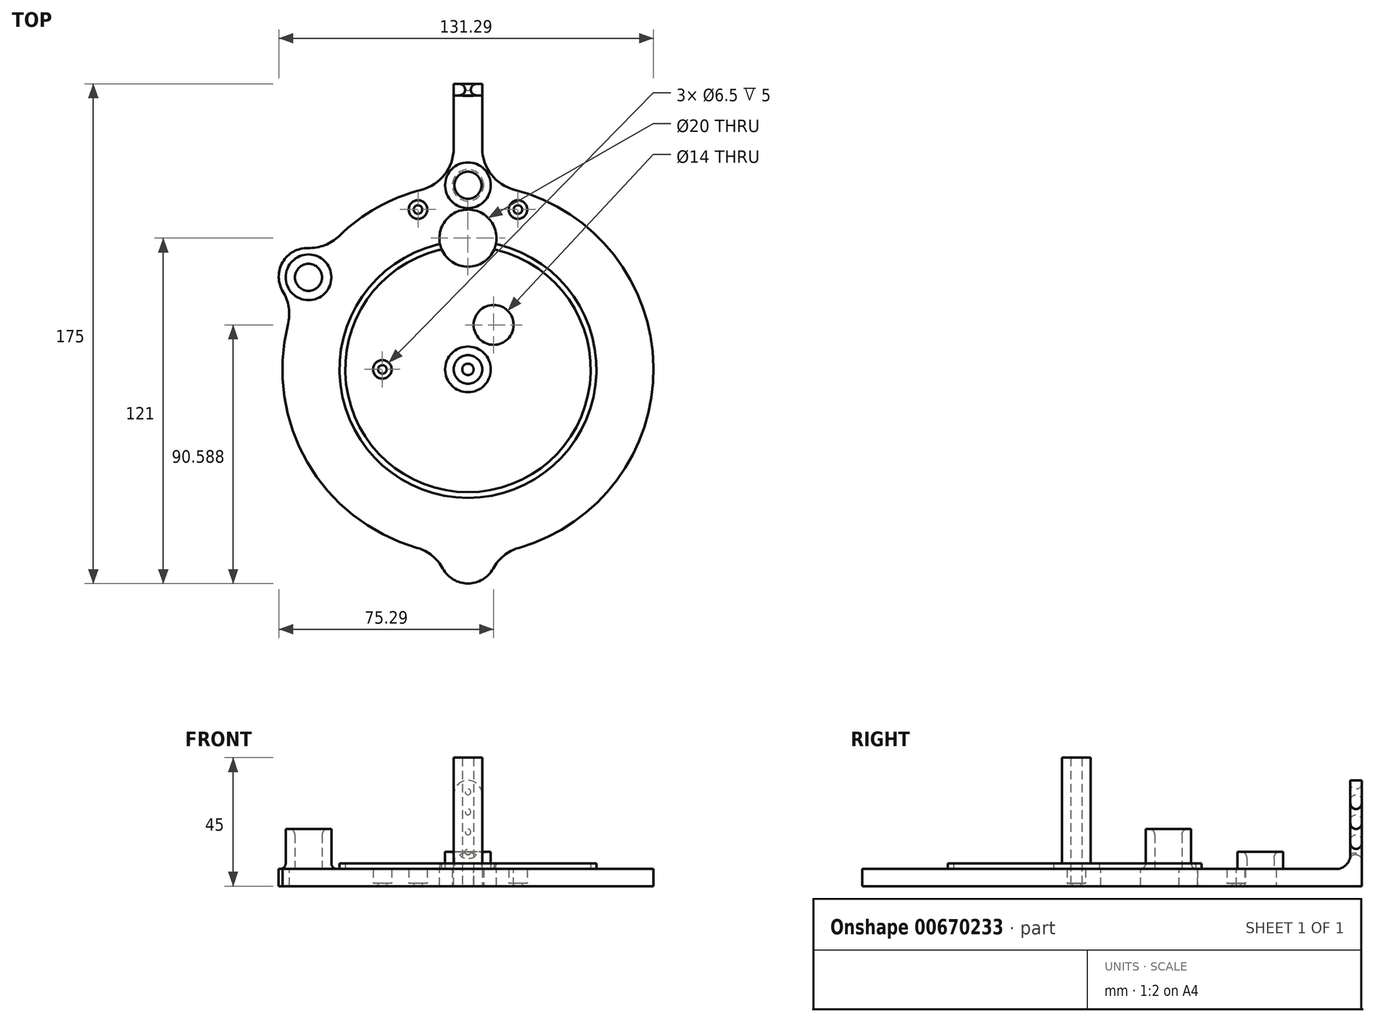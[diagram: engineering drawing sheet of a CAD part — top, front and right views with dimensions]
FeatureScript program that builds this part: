
annotation { "Feature Type Name" : "Feature", "Feature Type Description" : "" }
export const myFeature = defineFeature(function(context is Context, id is Id, definition is map)
    precondition{}
    {
        {
            var Q0;
            Q0=qCreatedBy(makeId("Top.planeOp"),FACE);
            var sketch = newSketch(context, id + "F0", { "sketchPlane" : qUnion([Q0])});
            skCircle(sketch, "E0", {"center": v(0, 0) * mm, "radius": 100 * mm, "construction": true});
            skCircle(sketch, "E1", {"center": v(0, 0) * mm, "radius": 65 * mm});
            skLineSegment(sketch, "E2", {"start": v(0, 0) * mm, "end": v(-56.3, 32.5) * mm, "construction": true});
            skCircle(sketch, "E3", {"center": v(-56.3, 32.5) * mm, "radius": 10 * mm});
            skCircle(sketch, "E4", {"center": v(0, -65) * mm, "radius": 10 * mm});
            skLineSegment(sketch, "E5", {"start": v(0, -65) * mm, "end": v(0, 0) * mm, "construction": true});
            skSolve(sketch);
        }
        {
            var Q0;
            Q0 = qSketchRegion(id + "F0", true);
            extrude(context, id + "F1", {"entities" : qUnion([Q0]), "depth" : 6 * mm, "offsetDistance" : 25 * mm});
        }
        {
            var Q0;
            Q0=qCreatedBy(makeId("Top.planeOp"),FACE);
            var sketch = newSketch(context, id + "F2", { "sketchPlane" : qUnion([Q0])});
            skCircle(sketch, "E6", {"center": v(0, 0) * mm, "radius": 5 * mm});
            skSolve(sketch);
        }
        {
            var Q0;
            Q0 = qSketchRegion(id + "F2", true);
            extrude(context, id + "F3", {"entities" : qUnion([Q0]), "operationType" : NewBodyOperationType.ADD, "depth" : 45 * mm, "offsetDistance" : 25 * mm});
        }
        {
            var Q0;
            Q0=qCreatedBy(makeId("Top.planeOp"),FACE);
            var sketch = newSketch(context, id + "F4", { "sketchPlane" : qUnion([Q0])});
            skCircle(sketch, "E7", {"center": v(0, 0) * mm, "radius": 2 * mm});
            skSolve(sketch);
        }
        {
            var Q0;
            Q0 = qSketchRegion(id + "F4", true);
            extrude(context, id + "F5", {"entities" : qUnion([Q0]), "operationType" : NewBodyOperationType.REMOVE, "depth" : 100 * mm, "offsetDistance" : 25 * mm});
        }
        {
            var Q0;
            Q0=qCreatedBy(makeId("Right.planeOp"),FACE);
            var sketch = newSketch(context, id + "F6", { "sketchPlane" : qUnion([Q0])});
            skLineSegment(sketch, "E8", {"start": v(32.02, 0) * mm, "end": v(100, 0) * mm});
            skLineSegment(sketch, "E9", {"start": v(100, 0) * mm, "end": v(100, 37) * mm});
            skPoint(sketch, "E10.visualSharp", {"position": v(100, 0) * mm});
            skLineSegment(sketch, "E10.filletArc", {"start": v(100, 0) * mm, "end": v(100, 0) * mm});
            skLineSegment(sketch, "E11", {"start": v(32.02, 0) * mm, "end": v(32.02, 6) * mm});
            skLineSegment(sketch, "E12", {"start": v(32.02, 6) * mm, "end": v(91, 6) * mm});
            skLineSegment(sketch, "E13", {"start": v(96, 11) * mm, "end": v(96, 37) * mm});
            skLineSegment(sketch, "E14", {"start": v(96, 37) * mm, "end": v(100, 37) * mm});
            skPoint(sketch, "E15.visualSharp", {"position": v(96, 6) * mm});
            skArc(sketch, "E15.filletArc", {"start": v(91, 6) * mm, "mid": v(94.54, 7.46) * mm, "end": v(96, 11) * mm});
            skSolve(sketch);
        }
        {
            var Q0;
            Q0=makeQuery(id+"F6.imprint","IMPRINT",FACE,{"disambiguationData":[TD([[makeQuery(id+"F6.imprint","IMPRINT",EDGE,{"derivedFrom":sQuery(id+"F6.wireOp",EDGE,"E8")}),1.0]])]});
            extrude(context, id + "F7", {"entities" : qUnion([Q0]), "operationType" : NewBodyOperationType.ADD, "endBound" : BoundingType.SYMMETRIC, "depth" : 10 * mm, "offsetDistance" : 25 * mm});
        }
        {
            var Q0;
            Q0=qCreatedBy(makeId("Front.planeOp"),FACE);
            var sketch = newSketch(context, id + "F8", { "sketchPlane" : qUnion([Q0])});
            skCircle(sketch, "E16", {"center": v(0, 12) * mm, "radius": 1 * mm});
            skCircle(sketch, "E17", {"center": v(0, 19) * mm, "radius": 1 * mm});
            skCircle(sketch, "E18", {"center": v(0, 26) * mm, "radius": 1 * mm});
            skCircle(sketch, "E19", {"center": v(0, 33) * mm, "radius": 1 * mm});
            skSolve(sketch);
        }
        {
            var Q0;
            Q0 = qSketchRegion(id + "F8", true);
            extrude(context, id + "F9", {"entities" : qUnion([Q0]), "operationType" : NewBodyOperationType.REMOVE, "oppositeDirection" : true, "depth" : 200 * mm, "offsetDistance" : 25 * mm, "hasSecondDirection" : true, "secondDirectionOppositeDirection" : true, "secondDirectionDepth" : 50 * mm});
        }
        {
            var Q0;
            Q0=makeQuery(id+"F7.opExtrude","CAP_EDGE",EDGE,{"disambiguationData":[OSD([sQuery(id+"F6.wireOp",EDGE,"E14")])],"isStart":true});
            var Q1;
            Q1=makeQuery(id+"F7.opExtrude","CAP_EDGE",EDGE,{"disambiguationData":[OSD([sQuery(id+"F6.wireOp",EDGE,"E14")])],"isStart":false});
            var Q2;
            Q2=makeQuery(id+"FA8SAaLpnDRHzi7_1.2.F7.opExtrude","CAP_EDGE",EDGE,{"disambiguationData":[OSD([sQuery(id+"F6.wireOp",EDGE,"E14")])],"isStart":true});
            var Q3;
            Q3=makeQuery(id+"FA8SAaLpnDRHzi7_1.2.F7.opExtrude","CAP_EDGE",EDGE,{"disambiguationData":[OSD([sQuery(id+"F6.wireOp",EDGE,"E14")])],"isStart":false});
            var Q4;
            Q4=makeQuery(id+"FA8SAaLpnDRHzi7_1.1.F7.opExtrude","CAP_EDGE",EDGE,{"disambiguationData":[OSD([sQuery(id+"F6.wireOp",EDGE,"E14")])],"isStart":true});
            var Q5;
            Q5=makeQuery(id+"FA8SAaLpnDRHzi7_1.1.F7.opExtrude","CAP_EDGE",EDGE,{"disambiguationData":[OSD([sQuery(id+"F6.wireOp",EDGE,"E14")])],"isStart":false});
            fillet(context, id + "F10", {"entities" : qUnion([Q0, Q1, Q2, Q3, Q4, Q5]), "radius" : 5 * mm, "tangentPropagation" : true, "allowEdgeOverflow" : false});
        }
        {
            var Q0;
            Q0=makeQuery(id+"FA8SAaLpnDRHzi7_1.1.F7.boolean.opBoolean","INTERSECT",EDGE,{"derivedFrom":[makeQuery(id+"F1.opExtrude","SWEPT_FACE",FACE,{"disambiguationData":[OSD([sQuery(id+"F0.wireOp",EDGE,"E1")])]}),makeQuery(id+"FA8SAaLpnDRHzi7_1.1.F7.opExtrude","CAP_FACE",FACE,{"disambiguationData":[OSD([sQuery(id+"F6.wireOp",EDGE,"E8"),sQuery(id+"F6.wireOp",EDGE,"E9"),sQuery(id+"F6.wireOp",EDGE,"E10.filletArc"),sQuery(id+"F6.wireOp",EDGE,"E11"),sQuery(id+"F6.wireOp",EDGE,"E12"),sQuery(id+"F6.wireOp",EDGE,"E13"),sQuery(id+"F6.wireOp",EDGE,"E14"),sQuery(id+"F6.wireOp",EDGE,"E15.filletArc")])],"isStart":true})]});
            var Q1;
            {var subQ0=sQuery(id+"F6.wireOp",EDGE,"E15.filletArc");var subQ1=sQuery(id+"F6.wireOp",EDGE,"E14");var subQ2=sQuery(id+"F6.wireOp",EDGE,"E13");var subQ3=sQuery(id+"F6.wireOp",EDGE,"E12");var subQ4=sQuery(id+"F6.wireOp",EDGE,"E11");var subQ5=sQuery(id+"F6.wireOp",EDGE,"E10.filletArc");var subQ6=sQuery(id+"F6.wireOp",EDGE,"E9");var subQ7=sQuery(id+"F6.wireOp",EDGE,"E8");var subQ8=sQuery(id+"F0.wireOp",EDGE,"E1");Q1=makeQuery(id+"FA8SAaLpnDRHzi7_1.2.F7.boolean.opBoolean","INTERSECT",EDGE,{"derivedFrom":[makeQuery(id+"FA8SAaLpnDRHzi7_1.1.F7.boolean.opBoolean","SPLIT",FACE,{"disambiguationData":[TD([makeQuery(id+"F7.opExtrude","CAP_FACE",FACE,{"disambiguationData":[OSD([subQ7,subQ6,subQ5,subQ4,subQ3,subQ2,subQ1,subQ0])],"isStart":false})])],"derivedFrom":makeQuery(id+"F1.opExtrude","SWEPT_FACE",FACE,{"disambiguationData":[OSD([subQ8])]})}),makeQuery(id+"FA8SAaLpnDRHzi7_1.2.F7.opExtrude","CAP_FACE",FACE,{"disambiguationData":[OSD([subQ7,subQ6,subQ5,subQ4,subQ3,subQ2,subQ1,subQ0])],"isStart":false})]});}
            var Q2;
            {var subQ0=sQuery(id+"F6.wireOp",EDGE,"E15.filletArc");var subQ1=sQuery(id+"F6.wireOp",EDGE,"E14");var subQ2=sQuery(id+"F6.wireOp",EDGE,"E13");var subQ3=sQuery(id+"F6.wireOp",EDGE,"E12");var subQ4=sQuery(id+"F6.wireOp",EDGE,"E11");var subQ5=sQuery(id+"F6.wireOp",EDGE,"E10.filletArc");var subQ6=sQuery(id+"F6.wireOp",EDGE,"E9");var subQ7=sQuery(id+"F6.wireOp",EDGE,"E8");var subQ8=sQuery(id+"F0.wireOp",EDGE,"E1");Q2=makeQuery(id+"FA8SAaLpnDRHzi7_1.2.F7.boolean.opBoolean","INTERSECT",EDGE,{"derivedFrom":[makeQuery(id+"FA8SAaLpnDRHzi7_1.1.F7.boolean.opBoolean","SPLIT",FACE,{"disambiguationData":[TD([makeQuery(id+"F7.opExtrude","CAP_FACE",FACE,{"disambiguationData":[OSD([subQ7,subQ6,subQ5,subQ4,subQ3,subQ2,subQ1,subQ0])],"isStart":false})])],"derivedFrom":makeQuery(id+"F1.opExtrude","SWEPT_FACE",FACE,{"disambiguationData":[OSD([subQ8])]})}),makeQuery(id+"FA8SAaLpnDRHzi7_1.2.F7.opExtrude","CAP_FACE",FACE,{"disambiguationData":[OSD([subQ7,subQ6,subQ5,subQ4,subQ3,subQ2,subQ1,subQ0])],"isStart":true})]});}
            var Q3;
            Q3=makeQuery(id+"F7.boolean.opBoolean","INTERSECT",EDGE,{"derivedFrom":[makeQuery(id+"F1.opExtrude","SWEPT_FACE",FACE,{"disambiguationData":[OSD([sQuery(id+"F0.wireOp",EDGE,"E1")])]}),makeQuery(id+"F7.opExtrude","CAP_FACE",FACE,{"disambiguationData":[OSD([sQuery(id+"F6.wireOp",EDGE,"E8"),sQuery(id+"F6.wireOp",EDGE,"E9"),sQuery(id+"F6.wireOp",EDGE,"E10.filletArc"),sQuery(id+"F6.wireOp",EDGE,"E11"),sQuery(id+"F6.wireOp",EDGE,"E12"),sQuery(id+"F6.wireOp",EDGE,"E13"),sQuery(id+"F6.wireOp",EDGE,"E14"),sQuery(id+"F6.wireOp",EDGE,"E15.filletArc")])],"isStart":false})]});
            var Q4;
            Q4=makeQuery(id+"F7.boolean.opBoolean","INTERSECT",EDGE,{"derivedFrom":[makeQuery(id+"F1.opExtrude","SWEPT_FACE",FACE,{"disambiguationData":[OSD([sQuery(id+"F0.wireOp",EDGE,"E1")])]}),makeQuery(id+"F7.opExtrude","CAP_FACE",FACE,{"disambiguationData":[OSD([sQuery(id+"F6.wireOp",EDGE,"E8"),sQuery(id+"F6.wireOp",EDGE,"E9"),sQuery(id+"F6.wireOp",EDGE,"E10.filletArc"),sQuery(id+"F6.wireOp",EDGE,"E11"),sQuery(id+"F6.wireOp",EDGE,"E12"),sQuery(id+"F6.wireOp",EDGE,"E13"),sQuery(id+"F6.wireOp",EDGE,"E14"),sQuery(id+"F6.wireOp",EDGE,"E15.filletArc")])],"isStart":true})]});
            var Q5;
            Q5=makeQuery(id+"FA8SAaLpnDRHzi7_1.1.F7.boolean.opBoolean","INTERSECT",EDGE,{"derivedFrom":[makeQuery(id+"F1.opExtrude","SWEPT_FACE",FACE,{"disambiguationData":[OSD([sQuery(id+"F0.wireOp",EDGE,"E1")])]}),makeQuery(id+"FA8SAaLpnDRHzi7_1.1.F7.opExtrude","CAP_FACE",FACE,{"disambiguationData":[OSD([sQuery(id+"F6.wireOp",EDGE,"E8"),sQuery(id+"F6.wireOp",EDGE,"E9"),sQuery(id+"F6.wireOp",EDGE,"E10.filletArc"),sQuery(id+"F6.wireOp",EDGE,"E11"),sQuery(id+"F6.wireOp",EDGE,"E12"),sQuery(id+"F6.wireOp",EDGE,"E13"),sQuery(id+"F6.wireOp",EDGE,"E14"),sQuery(id+"F6.wireOp",EDGE,"E15.filletArc")])],"isStart":false})]});
            var Q6;
            {var subQ0=sQuery(id+"F0.wireOp",EDGE,"E3");var subQ1=sQuery(id+"F0.wireOp",EDGE,"E1");Q6=makeQuery(id+"F1.opExtrude","SWEPT_EDGE",EDGE,{"disambiguationData":[OSD([subQ1,subQ0]),TDD([makeQuery(id+"F0.imprint","INTERSECT",VERTEX,{"disambiguationData":[OD(1.0)],"derivedFrom":[subQ1,subQ0]})])]});}
            var Q7;
            {var subQ0=sQuery(id+"F0.wireOp",EDGE,"E3");var subQ1=sQuery(id+"F0.wireOp",EDGE,"E1");Q7=makeQuery(id+"F1.opExtrude","SWEPT_EDGE",EDGE,{"disambiguationData":[OSD([subQ1,subQ0]),TDD([makeQuery(id+"F0.imprint","INTERSECT",VERTEX,{"disambiguationData":[OD(0.0)],"derivedFrom":[subQ1,subQ0]})])]});}
            var Q8;
            {var subQ0=sQuery(id+"F0.wireOp",EDGE,"E4");var subQ1=sQuery(id+"F0.wireOp",EDGE,"E1");Q8=makeQuery(id+"F1.opExtrude","SWEPT_EDGE",EDGE,{"disambiguationData":[OSD([subQ1,subQ0]),TDD([makeQuery(id+"F0.imprint","INTERSECT",VERTEX,{"disambiguationData":[OD(0.0)],"derivedFrom":[subQ1,subQ0]})])]});}
            var Q9;
            {var subQ0=sQuery(id+"F0.wireOp",EDGE,"E4");var subQ1=sQuery(id+"F0.wireOp",EDGE,"E1");Q9=makeQuery(id+"F1.opExtrude","SWEPT_EDGE",EDGE,{"disambiguationData":[OSD([subQ1,subQ0]),TDD([makeQuery(id+"F0.imprint","INTERSECT",VERTEX,{"disambiguationData":[OD(1.0)],"derivedFrom":[subQ1,subQ0]})])]});}
            fillet(context, id + "F11", {"entities" : qUnion([Q0, Q1, Q2, Q3, Q4, Q5, Q6, Q7, Q8, Q9]), "radius" : 15 * mm, "tangentPropagation" : true, "allowEdgeOverflow" : false});
        }
        {
            var Q0;
            Q0=qCreatedBy(makeId("Top.planeOp"),FACE);
            var sketch = newSketch(context, id + "F12", { "sketchPlane" : qUnion([Q0])});
            skCircle(sketch, "E20", {"center": v(0, 64.5) * mm, "radius": 5.5 * mm});
            skCircle(sketch, "E21", {"center": v(-17.5, 56) * mm, "radius": 1.5 * mm});
            skCircle(sketch, "E22", {"center": v(17.5, 56) * mm, "radius": 1.5 * mm});
            skSolve(sketch);
        }
        {
            var Q0;
            Q0 = qSketchRegion(id + "F12", true);
            extrude(context, id + "F13", {"entities" : qUnion([Q0]), "operationType" : NewBodyOperationType.REMOVE, "depth" : 25 * mm, "offsetDistance" : 25 * mm});
        }
        {
            var Q0;
            Q0=qCreatedBy(makeId("Top.planeOp"),FACE);
            var sketch = newSketch(context, id + "F14", { "sketchPlane" : qUnion([Q0])});
            skCircle(sketch, "E23", {"center": v(0, 64.5) * mm, "radius": 4.75 * mm, "construction": true});
            skCircle(sketch, "E24", {"center": v(-17.5, 56) * mm, "radius": 1.5 * mm, "construction": true});
            skCircle(sketch, "E25", {"center": v(17.5, 56) * mm, "radius": 1.5 * mm, "construction": true});
            skCircle(sketch, "E26.cCircle", {"center": v(-17.5, 56) * mm, "radius": 3.25 * mm});
            skCircle(sketch, "E27.cCircle", {"center": v(17.5, 56) * mm, "radius": 3.25 * mm});
            skCircle(sketch, "E28", {"center": v(0, 0) * mm, "radius": 58.67 * mm, "construction": true});
            skSolve(sketch);
        }
        {
            var Q0;
            Q0 = qSketchRegion(id + "F14", true);
            extrude(context, id + "F15", {"entities" : qUnion([Q0]), "operationType" : NewBodyOperationType.REMOVE, "depth" : 25 * mm, "offsetDistance" : 25 * mm, "hasSecondDirection" : true, "secondDirectionOppositeDirection" : false, "secondDirectionDepth" : 1 * mm});
        }
        {
            var Q0;
            Q0=makeQuery(id+"FA8SAaLpnDRHzi7_1.2.F9.boolean.opBoolean","INTERSECT",EDGE,{"derivedFrom":[makeQuery(id+"FA8SAaLpnDRHzi7_1.2.F7.opExtrude","SWEPT_FACE",FACE,{"disambiguationData":[OSD([sQuery(id+"F6.wireOp",EDGE,"E13")])]}),makeQuery(id+"FA8SAaLpnDRHzi7_1.2.F9.opExtrude","SWEPT_FACE",FACE,{"disambiguationData":[OSD([sQuery(id+"F8.wireOp",EDGE,"E16")])]})]});
            var Q1;
            Q1=makeQuery(id+"FA8SAaLpnDRHzi7_1.2.F9.boolean.opBoolean","INTERSECT",EDGE,{"derivedFrom":[makeQuery(id+"FA8SAaLpnDRHzi7_1.2.F7.opExtrude","SWEPT_FACE",FACE,{"disambiguationData":[OSD([sQuery(id+"F6.wireOp",EDGE,"E13")])]}),makeQuery(id+"FA8SAaLpnDRHzi7_1.2.F9.opExtrude","SWEPT_FACE",FACE,{"disambiguationData":[OSD([sQuery(id+"F8.wireOp",EDGE,"E17")])]})]});
            var Q2;
            Q2=makeQuery(id+"FA8SAaLpnDRHzi7_1.2.F9.boolean.opBoolean","INTERSECT",EDGE,{"derivedFrom":[makeQuery(id+"FA8SAaLpnDRHzi7_1.2.F7.opExtrude","SWEPT_FACE",FACE,{"disambiguationData":[OSD([sQuery(id+"F6.wireOp",EDGE,"E13")])]}),makeQuery(id+"FA8SAaLpnDRHzi7_1.2.F9.opExtrude","SWEPT_FACE",FACE,{"disambiguationData":[OSD([sQuery(id+"F8.wireOp",EDGE,"E18")])]})]});
            var Q3;
            Q3=makeQuery(id+"FA8SAaLpnDRHzi7_1.2.F9.boolean.opBoolean","INTERSECT",EDGE,{"derivedFrom":[makeQuery(id+"FA8SAaLpnDRHzi7_1.2.F7.opExtrude","SWEPT_FACE",FACE,{"disambiguationData":[OSD([sQuery(id+"F6.wireOp",EDGE,"E9")])]}),makeQuery(id+"FA8SAaLpnDRHzi7_1.2.F9.opExtrude","SWEPT_FACE",FACE,{"disambiguationData":[OSD([sQuery(id+"F8.wireOp",EDGE,"E16")])]})]});
            var Q4;
            Q4=makeQuery(id+"FA8SAaLpnDRHzi7_1.2.F9.boolean.opBoolean","INTERSECT",EDGE,{"derivedFrom":[makeQuery(id+"FA8SAaLpnDRHzi7_1.2.F7.opExtrude","SWEPT_FACE",FACE,{"disambiguationData":[OSD([sQuery(id+"F6.wireOp",EDGE,"E9")])]}),makeQuery(id+"FA8SAaLpnDRHzi7_1.2.F9.opExtrude","SWEPT_FACE",FACE,{"disambiguationData":[OSD([sQuery(id+"F8.wireOp",EDGE,"E17")])]})]});
            var Q5;
            Q5=makeQuery(id+"FA8SAaLpnDRHzi7_1.2.F9.boolean.opBoolean","INTERSECT",EDGE,{"derivedFrom":[makeQuery(id+"FA8SAaLpnDRHzi7_1.2.F7.opExtrude","SWEPT_FACE",FACE,{"disambiguationData":[OSD([sQuery(id+"F6.wireOp",EDGE,"E9")])]}),makeQuery(id+"FA8SAaLpnDRHzi7_1.2.F9.opExtrude","SWEPT_FACE",FACE,{"disambiguationData":[OSD([sQuery(id+"F8.wireOp",EDGE,"E18")])]})]});
            var Q6;
            Q6=makeQuery(id+"F9.boolean.opBoolean","INTERSECT",EDGE,{"derivedFrom":[makeQuery(id+"F7.opExtrude","SWEPT_FACE",FACE,{"disambiguationData":[OSD([sQuery(id+"F6.wireOp",EDGE,"E9")])]}),makeQuery(id+"F9.opExtrude","SWEPT_FACE",FACE,{"disambiguationData":[OSD([sQuery(id+"F8.wireOp",EDGE,"E16")])]})]});
            var Q7;
            Q7=makeQuery(id+"F9.boolean.opBoolean","INTERSECT",EDGE,{"derivedFrom":[makeQuery(id+"F7.opExtrude","SWEPT_FACE",FACE,{"disambiguationData":[OSD([sQuery(id+"F6.wireOp",EDGE,"E9")])]}),makeQuery(id+"F9.opExtrude","SWEPT_FACE",FACE,{"disambiguationData":[OSD([sQuery(id+"F8.wireOp",EDGE,"E17")])]})]});
            var Q8;
            Q8=makeQuery(id+"F9.boolean.opBoolean","INTERSECT",EDGE,{"derivedFrom":[makeQuery(id+"F7.opExtrude","SWEPT_FACE",FACE,{"disambiguationData":[OSD([sQuery(id+"F6.wireOp",EDGE,"E9")])]}),makeQuery(id+"F9.opExtrude","SWEPT_FACE",FACE,{"disambiguationData":[OSD([sQuery(id+"F8.wireOp",EDGE,"E18")])]})]});
            var Q9;
            Q9=makeQuery(id+"F9.boolean.opBoolean","INTERSECT",EDGE,{"derivedFrom":[makeQuery(id+"F7.opExtrude","SWEPT_FACE",FACE,{"disambiguationData":[OSD([sQuery(id+"F6.wireOp",EDGE,"E13")])]}),makeQuery(id+"F9.opExtrude","SWEPT_FACE",FACE,{"disambiguationData":[OSD([sQuery(id+"F8.wireOp",EDGE,"E18")])]})]});
            var Q10;
            Q10=makeQuery(id+"F9.boolean.opBoolean","INTERSECT",EDGE,{"derivedFrom":[makeQuery(id+"F7.opExtrude","SWEPT_FACE",FACE,{"disambiguationData":[OSD([sQuery(id+"F6.wireOp",EDGE,"E13")])]}),makeQuery(id+"F9.opExtrude","SWEPT_FACE",FACE,{"disambiguationData":[OSD([sQuery(id+"F8.wireOp",EDGE,"E17")])]})]});
            var Q11;
            Q11=makeQuery(id+"F9.boolean.opBoolean","INTERSECT",EDGE,{"derivedFrom":[makeQuery(id+"F7.opExtrude","SWEPT_FACE",FACE,{"disambiguationData":[OSD([sQuery(id+"F6.wireOp",EDGE,"E13")])]}),makeQuery(id+"F9.opExtrude","SWEPT_FACE",FACE,{"disambiguationData":[OSD([sQuery(id+"F8.wireOp",EDGE,"E16")])]})]});
            var Q12;
            Q12=makeQuery(id+"FA8SAaLpnDRHzi7_1.1.F9.boolean.opBoolean","INTERSECT",EDGE,{"derivedFrom":[makeQuery(id+"FA8SAaLpnDRHzi7_1.1.F7.opExtrude","SWEPT_FACE",FACE,{"disambiguationData":[OSD([sQuery(id+"F6.wireOp",EDGE,"E9")])]}),makeQuery(id+"FA8SAaLpnDRHzi7_1.1.F9.opExtrude","SWEPT_FACE",FACE,{"disambiguationData":[OSD([sQuery(id+"F8.wireOp",EDGE,"E16")])]})]});
            var Q13;
            Q13=makeQuery(id+"FA8SAaLpnDRHzi7_1.1.F9.boolean.opBoolean","INTERSECT",EDGE,{"derivedFrom":[makeQuery(id+"FA8SAaLpnDRHzi7_1.1.F7.opExtrude","SWEPT_FACE",FACE,{"disambiguationData":[OSD([sQuery(id+"F6.wireOp",EDGE,"E9")])]}),makeQuery(id+"FA8SAaLpnDRHzi7_1.1.F9.opExtrude","SWEPT_FACE",FACE,{"disambiguationData":[OSD([sQuery(id+"F8.wireOp",EDGE,"E17")])]})]});
            var Q14;
            Q14=makeQuery(id+"FA8SAaLpnDRHzi7_1.1.F9.boolean.opBoolean","INTERSECT",EDGE,{"derivedFrom":[makeQuery(id+"FA8SAaLpnDRHzi7_1.1.F7.opExtrude","SWEPT_FACE",FACE,{"disambiguationData":[OSD([sQuery(id+"F6.wireOp",EDGE,"E9")])]}),makeQuery(id+"FA8SAaLpnDRHzi7_1.1.F9.opExtrude","SWEPT_FACE",FACE,{"disambiguationData":[OSD([sQuery(id+"F8.wireOp",EDGE,"E18")])]})]});
            var Q15;
            Q15=makeQuery(id+"FA8SAaLpnDRHzi7_1.1.F9.boolean.opBoolean","INTERSECT",EDGE,{"derivedFrom":[makeQuery(id+"FA8SAaLpnDRHzi7_1.1.F7.opExtrude","SWEPT_FACE",FACE,{"disambiguationData":[OSD([sQuery(id+"F6.wireOp",EDGE,"E13")])]}),makeQuery(id+"FA8SAaLpnDRHzi7_1.1.F9.opExtrude","SWEPT_FACE",FACE,{"disambiguationData":[OSD([sQuery(id+"F8.wireOp",EDGE,"E16")])]})]});
            var Q16;
            Q16=makeQuery(id+"FA8SAaLpnDRHzi7_1.1.F9.boolean.opBoolean","INTERSECT",EDGE,{"derivedFrom":[makeQuery(id+"FA8SAaLpnDRHzi7_1.1.F7.opExtrude","SWEPT_FACE",FACE,{"disambiguationData":[OSD([sQuery(id+"F6.wireOp",EDGE,"E13")])]}),makeQuery(id+"FA8SAaLpnDRHzi7_1.1.F9.opExtrude","SWEPT_FACE",FACE,{"disambiguationData":[OSD([sQuery(id+"F8.wireOp",EDGE,"E17")])]})]});
            var Q17;
            Q17=makeQuery(id+"FA8SAaLpnDRHzi7_1.1.F9.boolean.opBoolean","INTERSECT",EDGE,{"derivedFrom":[makeQuery(id+"FA8SAaLpnDRHzi7_1.1.F7.opExtrude","SWEPT_FACE",FACE,{"disambiguationData":[OSD([sQuery(id+"F6.wireOp",EDGE,"E13")])]}),makeQuery(id+"FA8SAaLpnDRHzi7_1.1.F9.opExtrude","SWEPT_FACE",FACE,{"disambiguationData":[OSD([sQuery(id+"F8.wireOp",EDGE,"E18")])]})]});
            var Q18;
            Q18=makeQuery(id+"FA8SAaLpnDRHzi7_1.2.F9.boolean.opBoolean","COPY",FACE,{"derivedFrom":makeQuery(id+"FA8SAaLpnDRHzi7_1.2.F9.opExtrude","SWEPT_FACE",FACE,{"disambiguationData":[OSD([sQuery(id+"F8.wireOp",EDGE,"E19")])]})});
            var Q19;
            Q19=makeQuery(id+"F9.boolean.opBoolean","COPY",FACE,{"derivedFrom":makeQuery(id+"F9.opExtrude","SWEPT_FACE",FACE,{"disambiguationData":[OSD([sQuery(id+"F8.wireOp",EDGE,"E19")])]})});
            var Q20;
            Q20=makeQuery(id+"FA8SAaLpnDRHzi7_1.1.F9.boolean.opBoolean","COPY",FACE,{"derivedFrom":makeQuery(id+"FA8SAaLpnDRHzi7_1.1.F9.opExtrude","SWEPT_FACE",FACE,{"disambiguationData":[OSD([sQuery(id+"F8.wireOp",EDGE,"E19")])]})});
            fillet(context, id + "F16", {"entities" : qUnion([Q0, Q1, Q2, Q3, Q4, Q5, Q6, Q7, Q8, Q9, Q10, Q11, Q12, Q13, Q14, Q15, Q16, Q17, Q18, Q19, Q20]), "radius" : 2 * mm, "tangentPropagation" : true, "allowEdgeOverflow" : false});
        }
        {
            var Q0;
            {var subQ0=sQuery(id+"F6.wireOp",EDGE,"E12");Q0=makeQuery(id+"FA8SAaLpnDRHzi7_1.2.F7.boolean.opBoolean","MERGE",FACE,{"derivedFrom":[makeQuery(id+"FA8SAaLpnDRHzi7_1.1.F7.boolean.opBoolean","MERGE",FACE,{"derivedFrom":[makeQuery(id+"F7.boolean.opBoolean","MERGE",FACE,{"derivedFrom":[makeQuery(id+"F1.opExtrude","CAP_FACE",FACE,{"disambiguationData":[OSD([sQuery(id+"F0.wireOp",EDGE,"E1"),sQuery(id+"F0.wireOp",EDGE,"E3")])],"isStart":false}),makeQuery(id+"F7.opExtrude","SWEPT_FACE",FACE,{"disambiguationData":[OSD([subQ0])]})]}),makeQuery(id+"FA8SAaLpnDRHzi7_1.1.F7.opExtrude","SWEPT_FACE",FACE,{"disambiguationData":[OSD([subQ0])]})]}),makeQuery(id+"FA8SAaLpnDRHzi7_1.2.F7.opExtrude","SWEPT_FACE",FACE,{"disambiguationData":[OSD([subQ0])]})]});}
            var sketch = newSketch(context, id + "F17", { "sketchPlane" : qUnion([Q0])});
            skCircle(sketch, "E29", {"center": v(0, 0) * mm, "radius": 8 * mm});
            skCircle(sketch, "E30", {"center": v(0, 0) * mm, "radius": 5 * mm});
            skSolve(sketch);
        }
        {
            var Q0;
            Q0 = qSketchRegion(id + "F17", true);
            extrude(context, id + "F18", {"entities" : qUnion([Q0]), "operationType" : NewBodyOperationType.ADD, "depth" : 2 * mm, "offsetDistance" : 25 * mm});
        }
        {
            var Q0;
            Q0=qCreatedBy(makeId("Top.planeOp"),FACE);
            var sketch = newSketch(context, id + "F19", { "sketchPlane" : qUnion([Q0])});
            skCircle(sketch, "E31", {"center": v(-30, 0) * mm, "radius": 1.5 * mm});
            skSolve(sketch);
        }
        {
            var Q0;
            Q0 = qSketchRegion(id + "F19", true);
            extrude(context, id + "F20", {"entities" : qUnion([Q0]), "operationType" : NewBodyOperationType.REMOVE, "endBound" : BoundingType.SYMMETRIC, "depth" : 25 * mm, "offsetDistance" : 25 * mm});
        }
        {
            var Q0;
            Q0=qCreatedBy(makeId("Top.planeOp"),FACE);
            var sketch = newSketch(context, id + "F21", { "sketchPlane" : qUnion([Q0])});
            skCircle(sketch, "E32.cCircle", {"center": v(-30, 0) * mm, "radius": 3.25 * mm});
            skSolve(sketch);
        }
        {
            var Q0;
            Q0 = qSketchRegion(id + "F21", true);
            extrude(context, id + "F22", {"entities" : qUnion([Q0]), "operationType" : NewBodyOperationType.REMOVE, "depth" : 25 * mm, "offsetDistance" : 25 * mm, "hasSecondDirection" : true, "secondDirectionOppositeDirection" : false, "secondDirectionDepth" : 1 * mm});
        }
        {
            var Q0;
            {var subQ0=sQuery(id+"F6.wireOp",EDGE,"E12");Q0=makeQuery(id+"FA8SAaLpnDRHzi7_1.2.F7.boolean.opBoolean","MERGE",FACE,{"derivedFrom":[makeQuery(id+"FA8SAaLpnDRHzi7_1.1.F7.boolean.opBoolean","MERGE",FACE,{"derivedFrom":[makeQuery(id+"F7.boolean.opBoolean","MERGE",FACE,{"derivedFrom":[makeQuery(id+"F1.opExtrude","CAP_FACE",FACE,{"disambiguationData":[OSD([sQuery(id+"F0.wireOp",EDGE,"E1"),sQuery(id+"F0.wireOp",EDGE,"E3")])],"isStart":false}),makeQuery(id+"F7.opExtrude","SWEPT_FACE",FACE,{"disambiguationData":[OSD([subQ0])]})]}),makeQuery(id+"FA8SAaLpnDRHzi7_1.1.F7.opExtrude","SWEPT_FACE",FACE,{"disambiguationData":[OSD([subQ0])]})]}),makeQuery(id+"FA8SAaLpnDRHzi7_1.2.F7.opExtrude","SWEPT_FACE",FACE,{"disambiguationData":[OSD([subQ0])]})]});}
            var sketch = newSketch(context, id + "F23", { "sketchPlane" : qUnion([Q0])});
            skCircle(sketch, "E33", {"center": v(0, 0) * mm, "radius": 43 * mm});
            skCircle(sketch, "E34", {"center": v(0, 0) * mm, "radius": 45 * mm});
            skSolve(sketch);
        }
        {
            var Q0;
            Q0=makeQuery(id+"F23.imprint","IMPRINT",FACE,{"disambiguationData":[TD([[makeQuery(id+"F23.imprint","IMPRINT",EDGE,{"derivedFrom":sQuery(id+"F23.wireOp",EDGE,"E33")}),-1.0]])]});
            extrude(context, id + "F24", {"entities" : qUnion([Q0]), "operationType" : NewBodyOperationType.ADD, "depth" : 2 * mm, "offsetDistance" : 25 * mm});
        }
        {
            var Q0;
            Q0=qCreatedBy(makeId("Top.planeOp"),FACE);
            var sketch = newSketch(context, id + "F25", { "sketchPlane" : qUnion([Q0])});
            skCircle(sketch, "E35", {"center": v(0, 46) * mm, "radius": 10 * mm});
            skSolve(sketch);
        }
        {
            var Q0;
            Q0 = qSketchRegion(id + "F25", true);
            extrude(context, id + "F26", {"entities" : qUnion([Q0]), "operationType" : NewBodyOperationType.REMOVE, "endBound" : BoundingType.SYMMETRIC, "oppositeDirection" : true, "depth" : 25 * mm, "offsetDistance" : 25 * mm});
        }
        {
            var Q0;
            Q0=qCreatedBy(makeId("Top.planeOp"),FACE);
            var sketch = newSketch(context, id + "F27", { "sketchPlane" : qUnion([Q0])});
            skCircle(sketch, "E36", {"center": v(9, 15.59) * mm, "radius": 7 * mm});
            skLineSegment(sketch, "E37", {"start": v(0, 0) * mm, "end": v(9, 15.59) * mm});
            skSolve(sketch);
        }
        {
            var Q0;
            Q0 = qSketchRegion(id + "F27", true);
            extrude(context, id + "F28", {"entities" : qUnion([Q0]), "operationType" : NewBodyOperationType.REMOVE, "endBound" : BoundingType.SYMMETRIC, "oppositeDirection" : true, "depth" : 25 * mm, "offsetDistance" : 25 * mm});
        }
        {
            var Q0;
            {var subQ0=sQuery(id+"F25.wireOp",EDGE,"E35");var subQ1=sQuery(id+"F23.wireOp",EDGE,"E33");var subQ3=makeQuery(id+"F26.boolean.opBoolean","COPY",FACE,{"derivedFrom":makeQuery(id+"F26.opExtrude","SWEPT_FACE",FACE,{"disambiguationData":[OSD([subQ0])]})});var subQ4=sQuery(id+"F23.wireOp",EDGE,"E34");Q0=makeQuery(id+"FQKKJbCCAw18BRu_1.10.F26.boolean.opBoolean","INTERSECT",EDGE,{"disambiguationData":[OD(1.0)],"derivedFrom":[makeQuery(id+"FQKKJbCCAw18BRu_1.9.F26.boolean.opBoolean","SPLIT",FACE,{"disambiguationData":[TD([subQ3])],"derivedFrom":makeQuery(id+"FQKKJbCCAw18BRu_1.8.F26.boolean.opBoolean","SPLIT",FACE,{"disambiguationData":[TD([subQ3])],"derivedFrom":makeQuery(id+"FQKKJbCCAw18BRu_1.7.F26.boolean.opBoolean","SPLIT",FACE,{"disambiguationData":[TD([subQ3])],"derivedFrom":makeQuery(id+"FQKKJbCCAw18BRu_1.6.F26.boolean.opBoolean","SPLIT",FACE,{"disambiguationData":[TD([subQ3])],"derivedFrom":makeQuery(id+"FQKKJbCCAw18BRu_1.5.F26.boolean.opBoolean","SPLIT",FACE,{"disambiguationData":[TD([subQ3])],"derivedFrom":makeQuery(id+"FQKKJbCCAw18BRu_1.4.F26.boolean.opBoolean","SPLIT",FACE,{"disambiguationData":[TD([subQ3])],"derivedFrom":makeQuery(id+"FQKKJbCCAw18BRu_1.3.F26.boolean.opBoolean","SPLIT",FACE,{"disambiguationData":[TD([subQ3])],"derivedFrom":makeQuery(id+"FQKKJbCCAw18BRu_1.2.F26.boolean.opBoolean","SPLIT",FACE,{"disambiguationData":[TD([subQ3])],"derivedFrom":makeQuery(id+"FQKKJbCCAw18BRu_1.1.F26.boolean.opBoolean","SPLIT",FACE,{"disambiguationData":[OD(0.0)],"derivedFrom":makeQuery(id+"F24.opExtrude","CAP_FACE",FACE,{"disambiguationData":[OSD([subQ1,subQ4])],"isStart":false})})})})})})})})})}),makeQuery(id+"FQKKJbCCAw18BRu_1.10.F26.opExtrude","SWEPT_FACE",FACE,{"disambiguationData":[OSD([subQ0])]})]});}
            var Q1;
            {var subQ0=sQuery(id+"F25.wireOp",EDGE,"E35");var subQ1=sQuery(id+"F23.wireOp",EDGE,"E33");var subQ3=makeQuery(id+"F26.boolean.opBoolean","COPY",FACE,{"derivedFrom":makeQuery(id+"F26.opExtrude","SWEPT_FACE",FACE,{"disambiguationData":[OSD([subQ0])]})});var subQ4=sQuery(id+"F23.wireOp",EDGE,"E34");Q1=makeQuery(id+"FQKKJbCCAw18BRu_1.9.F26.boolean.opBoolean","INTERSECT",EDGE,{"disambiguationData":[OD(0.0)],"derivedFrom":[makeQuery(id+"FQKKJbCCAw18BRu_1.8.F26.boolean.opBoolean","SPLIT",FACE,{"disambiguationData":[TD([subQ3])],"derivedFrom":makeQuery(id+"FQKKJbCCAw18BRu_1.7.F26.boolean.opBoolean","SPLIT",FACE,{"disambiguationData":[TD([subQ3])],"derivedFrom":makeQuery(id+"FQKKJbCCAw18BRu_1.6.F26.boolean.opBoolean","SPLIT",FACE,{"disambiguationData":[TD([subQ3])],"derivedFrom":makeQuery(id+"FQKKJbCCAw18BRu_1.5.F26.boolean.opBoolean","SPLIT",FACE,{"disambiguationData":[TD([subQ3])],"derivedFrom":makeQuery(id+"FQKKJbCCAw18BRu_1.4.F26.boolean.opBoolean","SPLIT",FACE,{"disambiguationData":[TD([subQ3])],"derivedFrom":makeQuery(id+"FQKKJbCCAw18BRu_1.3.F26.boolean.opBoolean","SPLIT",FACE,{"disambiguationData":[TD([subQ3])],"derivedFrom":makeQuery(id+"FQKKJbCCAw18BRu_1.2.F26.boolean.opBoolean","SPLIT",FACE,{"disambiguationData":[TD([subQ3])],"derivedFrom":makeQuery(id+"FQKKJbCCAw18BRu_1.1.F26.boolean.opBoolean","SPLIT",FACE,{"disambiguationData":[OD(0.0)],"derivedFrom":makeQuery(id+"F24.opExtrude","CAP_FACE",FACE,{"disambiguationData":[OSD([subQ1,subQ4])],"isStart":false})})})})})})})})}),makeQuery(id+"FQKKJbCCAw18BRu_1.9.F26.opExtrude","SWEPT_FACE",FACE,{"disambiguationData":[OSD([subQ0])]})]});}
            var Q2;
            {var subQ0=sQuery(id+"F25.wireOp",EDGE,"E35");var subQ1=sQuery(id+"F23.wireOp",EDGE,"E33");var subQ3=makeQuery(id+"F26.boolean.opBoolean","COPY",FACE,{"derivedFrom":makeQuery(id+"F26.opExtrude","SWEPT_FACE",FACE,{"disambiguationData":[OSD([subQ0])]})});var subQ4=sQuery(id+"F23.wireOp",EDGE,"E34");Q2=makeQuery(id+"FQKKJbCCAw18BRu_1.10.F26.boolean.opBoolean","INTERSECT",EDGE,{"disambiguationData":[OD(0.0)],"derivedFrom":[makeQuery(id+"FQKKJbCCAw18BRu_1.9.F26.boolean.opBoolean","SPLIT",FACE,{"disambiguationData":[TD([subQ3])],"derivedFrom":makeQuery(id+"FQKKJbCCAw18BRu_1.8.F26.boolean.opBoolean","SPLIT",FACE,{"disambiguationData":[TD([subQ3])],"derivedFrom":makeQuery(id+"FQKKJbCCAw18BRu_1.7.F26.boolean.opBoolean","SPLIT",FACE,{"disambiguationData":[TD([subQ3])],"derivedFrom":makeQuery(id+"FQKKJbCCAw18BRu_1.6.F26.boolean.opBoolean","SPLIT",FACE,{"disambiguationData":[TD([subQ3])],"derivedFrom":makeQuery(id+"FQKKJbCCAw18BRu_1.5.F26.boolean.opBoolean","SPLIT",FACE,{"disambiguationData":[TD([subQ3])],"derivedFrom":makeQuery(id+"FQKKJbCCAw18BRu_1.4.F26.boolean.opBoolean","SPLIT",FACE,{"disambiguationData":[TD([subQ3])],"derivedFrom":makeQuery(id+"FQKKJbCCAw18BRu_1.3.F26.boolean.opBoolean","SPLIT",FACE,{"disambiguationData":[TD([subQ3])],"derivedFrom":makeQuery(id+"FQKKJbCCAw18BRu_1.2.F26.boolean.opBoolean","SPLIT",FACE,{"disambiguationData":[TD([subQ3])],"derivedFrom":makeQuery(id+"FQKKJbCCAw18BRu_1.1.F26.boolean.opBoolean","SPLIT",FACE,{"disambiguationData":[OD(0.0)],"derivedFrom":makeQuery(id+"F24.opExtrude","CAP_FACE",FACE,{"disambiguationData":[OSD([subQ1,subQ4])],"isStart":false})})})})})})})})})}),makeQuery(id+"FQKKJbCCAw18BRu_1.10.F26.opExtrude","SWEPT_FACE",FACE,{"disambiguationData":[OSD([subQ0])]})]});}
            var Q3;
            {var subQ0=sQuery(id+"F25.wireOp",EDGE,"E35");var subQ1=sQuery(id+"F23.wireOp",EDGE,"E33");var subQ3=makeQuery(id+"F26.boolean.opBoolean","COPY",FACE,{"derivedFrom":makeQuery(id+"F26.opExtrude","SWEPT_FACE",FACE,{"disambiguationData":[OSD([subQ0])]})});var subQ4=sQuery(id+"F23.wireOp",EDGE,"E34");Q3=makeQuery(id+"FQKKJbCCAw18BRu_1.11.F26.boolean.opBoolean","INTERSECT",EDGE,{"disambiguationData":[OD(1.0)],"derivedFrom":[makeQuery(id+"FQKKJbCCAw18BRu_1.10.F26.boolean.opBoolean","SPLIT",FACE,{"disambiguationData":[TD([subQ3])],"derivedFrom":makeQuery(id+"FQKKJbCCAw18BRu_1.9.F26.boolean.opBoolean","SPLIT",FACE,{"disambiguationData":[TD([subQ3])],"derivedFrom":makeQuery(id+"FQKKJbCCAw18BRu_1.8.F26.boolean.opBoolean","SPLIT",FACE,{"disambiguationData":[TD([subQ3])],"derivedFrom":makeQuery(id+"FQKKJbCCAw18BRu_1.7.F26.boolean.opBoolean","SPLIT",FACE,{"disambiguationData":[TD([subQ3])],"derivedFrom":makeQuery(id+"FQKKJbCCAw18BRu_1.6.F26.boolean.opBoolean","SPLIT",FACE,{"disambiguationData":[TD([subQ3])],"derivedFrom":makeQuery(id+"FQKKJbCCAw18BRu_1.5.F26.boolean.opBoolean","SPLIT",FACE,{"disambiguationData":[TD([subQ3])],"derivedFrom":makeQuery(id+"FQKKJbCCAw18BRu_1.4.F26.boolean.opBoolean","SPLIT",FACE,{"disambiguationData":[TD([subQ3])],"derivedFrom":makeQuery(id+"FQKKJbCCAw18BRu_1.3.F26.boolean.opBoolean","SPLIT",FACE,{"disambiguationData":[TD([subQ3])],"derivedFrom":makeQuery(id+"FQKKJbCCAw18BRu_1.2.F26.boolean.opBoolean","SPLIT",FACE,{"disambiguationData":[TD([subQ3])],"derivedFrom":makeQuery(id+"FQKKJbCCAw18BRu_1.1.F26.boolean.opBoolean","SPLIT",FACE,{"disambiguationData":[OD(0.0)],"derivedFrom":makeQuery(id+"F24.opExtrude","CAP_FACE",FACE,{"disambiguationData":[OSD([subQ1,subQ4])],"isStart":false})})})})})})})})})})}),makeQuery(id+"FQKKJbCCAw18BRu_1.11.F26.opExtrude","SWEPT_FACE",FACE,{"disambiguationData":[OSD([subQ0])]})]});}
            var Q4;
            {var subQ0=sQuery(id+"F25.wireOp",EDGE,"E35");var subQ1=sQuery(id+"F23.wireOp",EDGE,"E33");var subQ3=makeQuery(id+"F26.boolean.opBoolean","COPY",FACE,{"derivedFrom":makeQuery(id+"F26.opExtrude","SWEPT_FACE",FACE,{"disambiguationData":[OSD([subQ0])]})});var subQ4=sQuery(id+"F23.wireOp",EDGE,"E34");Q4=makeQuery(id+"FQKKJbCCAw18BRu_1.11.F26.boolean.opBoolean","INTERSECT",EDGE,{"disambiguationData":[OD(0.0)],"derivedFrom":[makeQuery(id+"FQKKJbCCAw18BRu_1.10.F26.boolean.opBoolean","SPLIT",FACE,{"disambiguationData":[TD([subQ3])],"derivedFrom":makeQuery(id+"FQKKJbCCAw18BRu_1.9.F26.boolean.opBoolean","SPLIT",FACE,{"disambiguationData":[TD([subQ3])],"derivedFrom":makeQuery(id+"FQKKJbCCAw18BRu_1.8.F26.boolean.opBoolean","SPLIT",FACE,{"disambiguationData":[TD([subQ3])],"derivedFrom":makeQuery(id+"FQKKJbCCAw18BRu_1.7.F26.boolean.opBoolean","SPLIT",FACE,{"disambiguationData":[TD([subQ3])],"derivedFrom":makeQuery(id+"FQKKJbCCAw18BRu_1.6.F26.boolean.opBoolean","SPLIT",FACE,{"disambiguationData":[TD([subQ3])],"derivedFrom":makeQuery(id+"FQKKJbCCAw18BRu_1.5.F26.boolean.opBoolean","SPLIT",FACE,{"disambiguationData":[TD([subQ3])],"derivedFrom":makeQuery(id+"FQKKJbCCAw18BRu_1.4.F26.boolean.opBoolean","SPLIT",FACE,{"disambiguationData":[TD([subQ3])],"derivedFrom":makeQuery(id+"FQKKJbCCAw18BRu_1.3.F26.boolean.opBoolean","SPLIT",FACE,{"disambiguationData":[TD([subQ3])],"derivedFrom":makeQuery(id+"FQKKJbCCAw18BRu_1.2.F26.boolean.opBoolean","SPLIT",FACE,{"disambiguationData":[TD([subQ3])],"derivedFrom":makeQuery(id+"FQKKJbCCAw18BRu_1.1.F26.boolean.opBoolean","SPLIT",FACE,{"disambiguationData":[OD(0.0)],"derivedFrom":makeQuery(id+"F24.opExtrude","CAP_FACE",FACE,{"disambiguationData":[OSD([subQ1,subQ4])],"isStart":false})})})})})})})})})})}),makeQuery(id+"FQKKJbCCAw18BRu_1.11.F26.opExtrude","SWEPT_FACE",FACE,{"disambiguationData":[OSD([subQ0])]})]});}
            var Q5;
            Q5=makeQuery(id+"F26.boolean.opBoolean","INTERSECT",EDGE,{"disambiguationData":[OD(0.0)],"derivedFrom":[makeQuery(id+"F24.opExtrude","CAP_FACE",FACE,{"disambiguationData":[OSD([sQuery(id+"F23.wireOp",EDGE,"E33"),sQuery(id+"F23.wireOp",EDGE,"E34")])],"isStart":false}),makeQuery(id+"F26.opExtrude","SWEPT_FACE",FACE,{"disambiguationData":[OSD([sQuery(id+"F25.wireOp",EDGE,"E35")])]})]});
            var Q6;
            Q6=makeQuery(id+"F26.boolean.opBoolean","INTERSECT",EDGE,{"disambiguationData":[OD(1.0)],"derivedFrom":[makeQuery(id+"F24.opExtrude","CAP_FACE",FACE,{"disambiguationData":[OSD([sQuery(id+"F23.wireOp",EDGE,"E33"),sQuery(id+"F23.wireOp",EDGE,"E34")])],"isStart":false}),makeQuery(id+"F26.opExtrude","SWEPT_FACE",FACE,{"disambiguationData":[OSD([sQuery(id+"F25.wireOp",EDGE,"E35")])]})]});
            var Q7;
            Q7=makeQuery(id+"FQKKJbCCAw18BRu_1.1.F26.boolean.opBoolean","INTERSECT",EDGE,{"disambiguationData":[OD(1.0)],"derivedFrom":[makeQuery(id+"F24.opExtrude","CAP_FACE",FACE,{"disambiguationData":[OSD([sQuery(id+"F23.wireOp",EDGE,"E33"),sQuery(id+"F23.wireOp",EDGE,"E34")])],"isStart":false}),makeQuery(id+"FQKKJbCCAw18BRu_1.1.F26.opExtrude","SWEPT_FACE",FACE,{"disambiguationData":[OSD([sQuery(id+"F25.wireOp",EDGE,"E35")])]})]});
            var Q8;
            Q8=makeQuery(id+"FQKKJbCCAw18BRu_1.1.F26.boolean.opBoolean","INTERSECT",EDGE,{"disambiguationData":[OD(0.0)],"derivedFrom":[makeQuery(id+"F24.opExtrude","CAP_FACE",FACE,{"disambiguationData":[OSD([sQuery(id+"F23.wireOp",EDGE,"E33"),sQuery(id+"F23.wireOp",EDGE,"E34")])],"isStart":false}),makeQuery(id+"FQKKJbCCAw18BRu_1.1.F26.opExtrude","SWEPT_FACE",FACE,{"disambiguationData":[OSD([sQuery(id+"F25.wireOp",EDGE,"E35")])]})]});
            var Q9;
            Q9=makeQuery(id+"FQKKJbCCAw18BRu_1.2.F26.boolean.opBoolean","INTERSECT",EDGE,{"disambiguationData":[OD(1.0)],"derivedFrom":[makeQuery(id+"FQKKJbCCAw18BRu_1.1.F26.boolean.opBoolean","SPLIT",FACE,{"disambiguationData":[OD(0.0)],"derivedFrom":makeQuery(id+"F24.opExtrude","CAP_FACE",FACE,{"disambiguationData":[OSD([sQuery(id+"F23.wireOp",EDGE,"E33"),sQuery(id+"F23.wireOp",EDGE,"E34")])],"isStart":false})}),makeQuery(id+"FQKKJbCCAw18BRu_1.2.F26.opExtrude","SWEPT_FACE",FACE,{"disambiguationData":[OSD([sQuery(id+"F25.wireOp",EDGE,"E35")])]})]});
            var Q10;
            Q10=makeQuery(id+"FQKKJbCCAw18BRu_1.2.F26.boolean.opBoolean","INTERSECT",EDGE,{"disambiguationData":[OD(0.0)],"derivedFrom":[makeQuery(id+"FQKKJbCCAw18BRu_1.1.F26.boolean.opBoolean","SPLIT",FACE,{"disambiguationData":[OD(0.0)],"derivedFrom":makeQuery(id+"F24.opExtrude","CAP_FACE",FACE,{"disambiguationData":[OSD([sQuery(id+"F23.wireOp",EDGE,"E33"),sQuery(id+"F23.wireOp",EDGE,"E34")])],"isStart":false})}),makeQuery(id+"FQKKJbCCAw18BRu_1.2.F26.opExtrude","SWEPT_FACE",FACE,{"disambiguationData":[OSD([sQuery(id+"F25.wireOp",EDGE,"E35")])]})]});
            var Q11;
            {var subQ0=sQuery(id+"F25.wireOp",EDGE,"E35");var subQ1=sQuery(id+"F23.wireOp",EDGE,"E33");var subQ2=sQuery(id+"F23.wireOp",EDGE,"E34");Q11=makeQuery(id+"FQKKJbCCAw18BRu_1.3.F26.boolean.opBoolean","INTERSECT",EDGE,{"disambiguationData":[OD(1.0)],"derivedFrom":[makeQuery(id+"FQKKJbCCAw18BRu_1.2.F26.boolean.opBoolean","SPLIT",FACE,{"disambiguationData":[TD([makeQuery(id+"F26.boolean.opBoolean","COPY",FACE,{"derivedFrom":makeQuery(id+"F26.opExtrude","SWEPT_FACE",FACE,{"disambiguationData":[OSD([subQ0])]})})])],"derivedFrom":makeQuery(id+"FQKKJbCCAw18BRu_1.1.F26.boolean.opBoolean","SPLIT",FACE,{"disambiguationData":[OD(0.0)],"derivedFrom":makeQuery(id+"F24.opExtrude","CAP_FACE",FACE,{"disambiguationData":[OSD([subQ1,subQ2])],"isStart":false})})}),makeQuery(id+"FQKKJbCCAw18BRu_1.3.F26.opExtrude","SWEPT_FACE",FACE,{"disambiguationData":[OSD([subQ0])]})]});}
            var Q12;
            {var subQ0=sQuery(id+"F25.wireOp",EDGE,"E35");var subQ1=sQuery(id+"F23.wireOp",EDGE,"E33");var subQ2=sQuery(id+"F23.wireOp",EDGE,"E34");Q12=makeQuery(id+"FQKKJbCCAw18BRu_1.3.F26.boolean.opBoolean","INTERSECT",EDGE,{"disambiguationData":[OD(0.0)],"derivedFrom":[makeQuery(id+"FQKKJbCCAw18BRu_1.2.F26.boolean.opBoolean","SPLIT",FACE,{"disambiguationData":[TD([makeQuery(id+"F26.boolean.opBoolean","COPY",FACE,{"derivedFrom":makeQuery(id+"F26.opExtrude","SWEPT_FACE",FACE,{"disambiguationData":[OSD([subQ0])]})})])],"derivedFrom":makeQuery(id+"FQKKJbCCAw18BRu_1.1.F26.boolean.opBoolean","SPLIT",FACE,{"disambiguationData":[OD(0.0)],"derivedFrom":makeQuery(id+"F24.opExtrude","CAP_FACE",FACE,{"disambiguationData":[OSD([subQ1,subQ2])],"isStart":false})})}),makeQuery(id+"FQKKJbCCAw18BRu_1.3.F26.opExtrude","SWEPT_FACE",FACE,{"disambiguationData":[OSD([subQ0])]})]});}
            var Q13;
            {var subQ0=sQuery(id+"F25.wireOp",EDGE,"E35");var subQ1=sQuery(id+"F23.wireOp",EDGE,"E33");var subQ3=makeQuery(id+"F26.boolean.opBoolean","COPY",FACE,{"derivedFrom":makeQuery(id+"F26.opExtrude","SWEPT_FACE",FACE,{"disambiguationData":[OSD([subQ0])]})});var subQ4=sQuery(id+"F23.wireOp",EDGE,"E34");Q13=makeQuery(id+"FQKKJbCCAw18BRu_1.4.F26.boolean.opBoolean","INTERSECT",EDGE,{"disambiguationData":[OD(1.0)],"derivedFrom":[makeQuery(id+"FQKKJbCCAw18BRu_1.3.F26.boolean.opBoolean","SPLIT",FACE,{"disambiguationData":[TD([subQ3])],"derivedFrom":makeQuery(id+"FQKKJbCCAw18BRu_1.2.F26.boolean.opBoolean","SPLIT",FACE,{"disambiguationData":[TD([subQ3])],"derivedFrom":makeQuery(id+"FQKKJbCCAw18BRu_1.1.F26.boolean.opBoolean","SPLIT",FACE,{"disambiguationData":[OD(0.0)],"derivedFrom":makeQuery(id+"F24.opExtrude","CAP_FACE",FACE,{"disambiguationData":[OSD([subQ1,subQ4])],"isStart":false})})})}),makeQuery(id+"FQKKJbCCAw18BRu_1.4.F26.opExtrude","SWEPT_FACE",FACE,{"disambiguationData":[OSD([subQ0])]})]});}
            var Q14;
            {var subQ0=sQuery(id+"F25.wireOp",EDGE,"E35");var subQ1=sQuery(id+"F23.wireOp",EDGE,"E33");var subQ3=makeQuery(id+"F26.boolean.opBoolean","COPY",FACE,{"derivedFrom":makeQuery(id+"F26.opExtrude","SWEPT_FACE",FACE,{"disambiguationData":[OSD([subQ0])]})});var subQ4=sQuery(id+"F23.wireOp",EDGE,"E34");Q14=makeQuery(id+"FQKKJbCCAw18BRu_1.4.F26.boolean.opBoolean","INTERSECT",EDGE,{"disambiguationData":[OD(0.0)],"derivedFrom":[makeQuery(id+"FQKKJbCCAw18BRu_1.3.F26.boolean.opBoolean","SPLIT",FACE,{"disambiguationData":[TD([subQ3])],"derivedFrom":makeQuery(id+"FQKKJbCCAw18BRu_1.2.F26.boolean.opBoolean","SPLIT",FACE,{"disambiguationData":[TD([subQ3])],"derivedFrom":makeQuery(id+"FQKKJbCCAw18BRu_1.1.F26.boolean.opBoolean","SPLIT",FACE,{"disambiguationData":[OD(0.0)],"derivedFrom":makeQuery(id+"F24.opExtrude","CAP_FACE",FACE,{"disambiguationData":[OSD([subQ1,subQ4])],"isStart":false})})})}),makeQuery(id+"FQKKJbCCAw18BRu_1.4.F26.opExtrude","SWEPT_FACE",FACE,{"disambiguationData":[OSD([subQ0])]})]});}
            var Q15;
            {var subQ0=sQuery(id+"F25.wireOp",EDGE,"E35");var subQ1=sQuery(id+"F23.wireOp",EDGE,"E33");var subQ3=makeQuery(id+"F26.boolean.opBoolean","COPY",FACE,{"derivedFrom":makeQuery(id+"F26.opExtrude","SWEPT_FACE",FACE,{"disambiguationData":[OSD([subQ0])]})});var subQ4=sQuery(id+"F23.wireOp",EDGE,"E34");Q15=makeQuery(id+"FQKKJbCCAw18BRu_1.5.F26.boolean.opBoolean","INTERSECT",EDGE,{"disambiguationData":[OD(1.0)],"derivedFrom":[makeQuery(id+"FQKKJbCCAw18BRu_1.4.F26.boolean.opBoolean","SPLIT",FACE,{"disambiguationData":[TD([subQ3])],"derivedFrom":makeQuery(id+"FQKKJbCCAw18BRu_1.3.F26.boolean.opBoolean","SPLIT",FACE,{"disambiguationData":[TD([subQ3])],"derivedFrom":makeQuery(id+"FQKKJbCCAw18BRu_1.2.F26.boolean.opBoolean","SPLIT",FACE,{"disambiguationData":[TD([subQ3])],"derivedFrom":makeQuery(id+"FQKKJbCCAw18BRu_1.1.F26.boolean.opBoolean","SPLIT",FACE,{"disambiguationData":[OD(0.0)],"derivedFrom":makeQuery(id+"F24.opExtrude","CAP_FACE",FACE,{"disambiguationData":[OSD([subQ1,subQ4])],"isStart":false})})})})}),makeQuery(id+"FQKKJbCCAw18BRu_1.5.F26.opExtrude","SWEPT_FACE",FACE,{"disambiguationData":[OSD([subQ0])]})]});}
            var Q16;
            {var subQ0=sQuery(id+"F25.wireOp",EDGE,"E35");var subQ1=sQuery(id+"F23.wireOp",EDGE,"E33");var subQ3=makeQuery(id+"F26.boolean.opBoolean","COPY",FACE,{"derivedFrom":makeQuery(id+"F26.opExtrude","SWEPT_FACE",FACE,{"disambiguationData":[OSD([subQ0])]})});var subQ4=sQuery(id+"F23.wireOp",EDGE,"E34");Q16=makeQuery(id+"FQKKJbCCAw18BRu_1.5.F26.boolean.opBoolean","INTERSECT",EDGE,{"disambiguationData":[OD(0.0)],"derivedFrom":[makeQuery(id+"FQKKJbCCAw18BRu_1.4.F26.boolean.opBoolean","SPLIT",FACE,{"disambiguationData":[TD([subQ3])],"derivedFrom":makeQuery(id+"FQKKJbCCAw18BRu_1.3.F26.boolean.opBoolean","SPLIT",FACE,{"disambiguationData":[TD([subQ3])],"derivedFrom":makeQuery(id+"FQKKJbCCAw18BRu_1.2.F26.boolean.opBoolean","SPLIT",FACE,{"disambiguationData":[TD([subQ3])],"derivedFrom":makeQuery(id+"FQKKJbCCAw18BRu_1.1.F26.boolean.opBoolean","SPLIT",FACE,{"disambiguationData":[OD(0.0)],"derivedFrom":makeQuery(id+"F24.opExtrude","CAP_FACE",FACE,{"disambiguationData":[OSD([subQ1,subQ4])],"isStart":false})})})})}),makeQuery(id+"FQKKJbCCAw18BRu_1.5.F26.opExtrude","SWEPT_FACE",FACE,{"disambiguationData":[OSD([subQ0])]})]});}
            var Q17;
            {var subQ0=sQuery(id+"F25.wireOp",EDGE,"E35");var subQ1=sQuery(id+"F23.wireOp",EDGE,"E33");var subQ3=makeQuery(id+"F26.boolean.opBoolean","COPY",FACE,{"derivedFrom":makeQuery(id+"F26.opExtrude","SWEPT_FACE",FACE,{"disambiguationData":[OSD([subQ0])]})});var subQ4=sQuery(id+"F23.wireOp",EDGE,"E34");Q17=makeQuery(id+"FQKKJbCCAw18BRu_1.6.F26.boolean.opBoolean","INTERSECT",EDGE,{"disambiguationData":[OD(1.0)],"derivedFrom":[makeQuery(id+"FQKKJbCCAw18BRu_1.5.F26.boolean.opBoolean","SPLIT",FACE,{"disambiguationData":[TD([subQ3])],"derivedFrom":makeQuery(id+"FQKKJbCCAw18BRu_1.4.F26.boolean.opBoolean","SPLIT",FACE,{"disambiguationData":[TD([subQ3])],"derivedFrom":makeQuery(id+"FQKKJbCCAw18BRu_1.3.F26.boolean.opBoolean","SPLIT",FACE,{"disambiguationData":[TD([subQ3])],"derivedFrom":makeQuery(id+"FQKKJbCCAw18BRu_1.2.F26.boolean.opBoolean","SPLIT",FACE,{"disambiguationData":[TD([subQ3])],"derivedFrom":makeQuery(id+"FQKKJbCCAw18BRu_1.1.F26.boolean.opBoolean","SPLIT",FACE,{"disambiguationData":[OD(0.0)],"derivedFrom":makeQuery(id+"F24.opExtrude","CAP_FACE",FACE,{"disambiguationData":[OSD([subQ1,subQ4])],"isStart":false})})})})})}),makeQuery(id+"FQKKJbCCAw18BRu_1.6.F26.opExtrude","SWEPT_FACE",FACE,{"disambiguationData":[OSD([subQ0])]})]});}
            var Q18;
            {var subQ0=sQuery(id+"F25.wireOp",EDGE,"E35");var subQ1=sQuery(id+"F23.wireOp",EDGE,"E33");var subQ3=makeQuery(id+"F26.boolean.opBoolean","COPY",FACE,{"derivedFrom":makeQuery(id+"F26.opExtrude","SWEPT_FACE",FACE,{"disambiguationData":[OSD([subQ0])]})});var subQ4=sQuery(id+"F23.wireOp",EDGE,"E34");Q18=makeQuery(id+"FQKKJbCCAw18BRu_1.6.F26.boolean.opBoolean","INTERSECT",EDGE,{"disambiguationData":[OD(0.0)],"derivedFrom":[makeQuery(id+"FQKKJbCCAw18BRu_1.5.F26.boolean.opBoolean","SPLIT",FACE,{"disambiguationData":[TD([subQ3])],"derivedFrom":makeQuery(id+"FQKKJbCCAw18BRu_1.4.F26.boolean.opBoolean","SPLIT",FACE,{"disambiguationData":[TD([subQ3])],"derivedFrom":makeQuery(id+"FQKKJbCCAw18BRu_1.3.F26.boolean.opBoolean","SPLIT",FACE,{"disambiguationData":[TD([subQ3])],"derivedFrom":makeQuery(id+"FQKKJbCCAw18BRu_1.2.F26.boolean.opBoolean","SPLIT",FACE,{"disambiguationData":[TD([subQ3])],"derivedFrom":makeQuery(id+"FQKKJbCCAw18BRu_1.1.F26.boolean.opBoolean","SPLIT",FACE,{"disambiguationData":[OD(0.0)],"derivedFrom":makeQuery(id+"F24.opExtrude","CAP_FACE",FACE,{"disambiguationData":[OSD([subQ1,subQ4])],"isStart":false})})})})})}),makeQuery(id+"FQKKJbCCAw18BRu_1.6.F26.opExtrude","SWEPT_FACE",FACE,{"disambiguationData":[OSD([subQ0])]})]});}
            var Q19;
            {var subQ0=sQuery(id+"F25.wireOp",EDGE,"E35");var subQ1=sQuery(id+"F23.wireOp",EDGE,"E33");var subQ3=makeQuery(id+"F26.boolean.opBoolean","COPY",FACE,{"derivedFrom":makeQuery(id+"F26.opExtrude","SWEPT_FACE",FACE,{"disambiguationData":[OSD([subQ0])]})});var subQ4=sQuery(id+"F23.wireOp",EDGE,"E34");Q19=makeQuery(id+"FQKKJbCCAw18BRu_1.7.F26.boolean.opBoolean","INTERSECT",EDGE,{"disambiguationData":[OD(1.0)],"derivedFrom":[makeQuery(id+"FQKKJbCCAw18BRu_1.6.F26.boolean.opBoolean","SPLIT",FACE,{"disambiguationData":[TD([subQ3])],"derivedFrom":makeQuery(id+"FQKKJbCCAw18BRu_1.5.F26.boolean.opBoolean","SPLIT",FACE,{"disambiguationData":[TD([subQ3])],"derivedFrom":makeQuery(id+"FQKKJbCCAw18BRu_1.4.F26.boolean.opBoolean","SPLIT",FACE,{"disambiguationData":[TD([subQ3])],"derivedFrom":makeQuery(id+"FQKKJbCCAw18BRu_1.3.F26.boolean.opBoolean","SPLIT",FACE,{"disambiguationData":[TD([subQ3])],"derivedFrom":makeQuery(id+"FQKKJbCCAw18BRu_1.2.F26.boolean.opBoolean","SPLIT",FACE,{"disambiguationData":[TD([subQ3])],"derivedFrom":makeQuery(id+"FQKKJbCCAw18BRu_1.1.F26.boolean.opBoolean","SPLIT",FACE,{"disambiguationData":[OD(0.0)],"derivedFrom":makeQuery(id+"F24.opExtrude","CAP_FACE",FACE,{"disambiguationData":[OSD([subQ1,subQ4])],"isStart":false})})})})})})}),makeQuery(id+"FQKKJbCCAw18BRu_1.7.F26.opExtrude","SWEPT_FACE",FACE,{"disambiguationData":[OSD([subQ0])]})]});}
            var Q20;
            {var subQ0=sQuery(id+"F25.wireOp",EDGE,"E35");var subQ1=sQuery(id+"F23.wireOp",EDGE,"E33");var subQ3=makeQuery(id+"F26.boolean.opBoolean","COPY",FACE,{"derivedFrom":makeQuery(id+"F26.opExtrude","SWEPT_FACE",FACE,{"disambiguationData":[OSD([subQ0])]})});var subQ4=sQuery(id+"F23.wireOp",EDGE,"E34");Q20=makeQuery(id+"FQKKJbCCAw18BRu_1.7.F26.boolean.opBoolean","INTERSECT",EDGE,{"disambiguationData":[OD(0.0)],"derivedFrom":[makeQuery(id+"FQKKJbCCAw18BRu_1.6.F26.boolean.opBoolean","SPLIT",FACE,{"disambiguationData":[TD([subQ3])],"derivedFrom":makeQuery(id+"FQKKJbCCAw18BRu_1.5.F26.boolean.opBoolean","SPLIT",FACE,{"disambiguationData":[TD([subQ3])],"derivedFrom":makeQuery(id+"FQKKJbCCAw18BRu_1.4.F26.boolean.opBoolean","SPLIT",FACE,{"disambiguationData":[TD([subQ3])],"derivedFrom":makeQuery(id+"FQKKJbCCAw18BRu_1.3.F26.boolean.opBoolean","SPLIT",FACE,{"disambiguationData":[TD([subQ3])],"derivedFrom":makeQuery(id+"FQKKJbCCAw18BRu_1.2.F26.boolean.opBoolean","SPLIT",FACE,{"disambiguationData":[TD([subQ3])],"derivedFrom":makeQuery(id+"FQKKJbCCAw18BRu_1.1.F26.boolean.opBoolean","SPLIT",FACE,{"disambiguationData":[OD(0.0)],"derivedFrom":makeQuery(id+"F24.opExtrude","CAP_FACE",FACE,{"disambiguationData":[OSD([subQ1,subQ4])],"isStart":false})})})})})})}),makeQuery(id+"FQKKJbCCAw18BRu_1.7.F26.opExtrude","SWEPT_FACE",FACE,{"disambiguationData":[OSD([subQ0])]})]});}
            var Q21;
            {var subQ0=sQuery(id+"F25.wireOp",EDGE,"E35");var subQ1=sQuery(id+"F23.wireOp",EDGE,"E33");var subQ3=makeQuery(id+"F26.boolean.opBoolean","COPY",FACE,{"derivedFrom":makeQuery(id+"F26.opExtrude","SWEPT_FACE",FACE,{"disambiguationData":[OSD([subQ0])]})});var subQ4=sQuery(id+"F23.wireOp",EDGE,"E34");Q21=makeQuery(id+"FQKKJbCCAw18BRu_1.8.F26.boolean.opBoolean","INTERSECT",EDGE,{"disambiguationData":[OD(1.0)],"derivedFrom":[makeQuery(id+"FQKKJbCCAw18BRu_1.7.F26.boolean.opBoolean","SPLIT",FACE,{"disambiguationData":[TD([subQ3])],"derivedFrom":makeQuery(id+"FQKKJbCCAw18BRu_1.6.F26.boolean.opBoolean","SPLIT",FACE,{"disambiguationData":[TD([subQ3])],"derivedFrom":makeQuery(id+"FQKKJbCCAw18BRu_1.5.F26.boolean.opBoolean","SPLIT",FACE,{"disambiguationData":[TD([subQ3])],"derivedFrom":makeQuery(id+"FQKKJbCCAw18BRu_1.4.F26.boolean.opBoolean","SPLIT",FACE,{"disambiguationData":[TD([subQ3])],"derivedFrom":makeQuery(id+"FQKKJbCCAw18BRu_1.3.F26.boolean.opBoolean","SPLIT",FACE,{"disambiguationData":[TD([subQ3])],"derivedFrom":makeQuery(id+"FQKKJbCCAw18BRu_1.2.F26.boolean.opBoolean","SPLIT",FACE,{"disambiguationData":[TD([subQ3])],"derivedFrom":makeQuery(id+"FQKKJbCCAw18BRu_1.1.F26.boolean.opBoolean","SPLIT",FACE,{"disambiguationData":[OD(0.0)],"derivedFrom":makeQuery(id+"F24.opExtrude","CAP_FACE",FACE,{"disambiguationData":[OSD([subQ1,subQ4])],"isStart":false})})})})})})})}),makeQuery(id+"FQKKJbCCAw18BRu_1.8.F26.opExtrude","SWEPT_FACE",FACE,{"disambiguationData":[OSD([subQ0])]})]});}
            var Q22;
            {var subQ0=sQuery(id+"F25.wireOp",EDGE,"E35");var subQ1=sQuery(id+"F23.wireOp",EDGE,"E33");var subQ3=makeQuery(id+"F26.boolean.opBoolean","COPY",FACE,{"derivedFrom":makeQuery(id+"F26.opExtrude","SWEPT_FACE",FACE,{"disambiguationData":[OSD([subQ0])]})});var subQ4=sQuery(id+"F23.wireOp",EDGE,"E34");Q22=makeQuery(id+"FQKKJbCCAw18BRu_1.8.F26.boolean.opBoolean","INTERSECT",EDGE,{"disambiguationData":[OD(0.0)],"derivedFrom":[makeQuery(id+"FQKKJbCCAw18BRu_1.7.F26.boolean.opBoolean","SPLIT",FACE,{"disambiguationData":[TD([subQ3])],"derivedFrom":makeQuery(id+"FQKKJbCCAw18BRu_1.6.F26.boolean.opBoolean","SPLIT",FACE,{"disambiguationData":[TD([subQ3])],"derivedFrom":makeQuery(id+"FQKKJbCCAw18BRu_1.5.F26.boolean.opBoolean","SPLIT",FACE,{"disambiguationData":[TD([subQ3])],"derivedFrom":makeQuery(id+"FQKKJbCCAw18BRu_1.4.F26.boolean.opBoolean","SPLIT",FACE,{"disambiguationData":[TD([subQ3])],"derivedFrom":makeQuery(id+"FQKKJbCCAw18BRu_1.3.F26.boolean.opBoolean","SPLIT",FACE,{"disambiguationData":[TD([subQ3])],"derivedFrom":makeQuery(id+"FQKKJbCCAw18BRu_1.2.F26.boolean.opBoolean","SPLIT",FACE,{"disambiguationData":[TD([subQ3])],"derivedFrom":makeQuery(id+"FQKKJbCCAw18BRu_1.1.F26.boolean.opBoolean","SPLIT",FACE,{"disambiguationData":[OD(0.0)],"derivedFrom":makeQuery(id+"F24.opExtrude","CAP_FACE",FACE,{"disambiguationData":[OSD([subQ1,subQ4])],"isStart":false})})})})})})})}),makeQuery(id+"FQKKJbCCAw18BRu_1.8.F26.opExtrude","SWEPT_FACE",FACE,{"disambiguationData":[OSD([subQ0])]})]});}
            var Q23;
            {var subQ0=sQuery(id+"F25.wireOp",EDGE,"E35");var subQ1=sQuery(id+"F23.wireOp",EDGE,"E33");var subQ3=makeQuery(id+"F26.boolean.opBoolean","COPY",FACE,{"derivedFrom":makeQuery(id+"F26.opExtrude","SWEPT_FACE",FACE,{"disambiguationData":[OSD([subQ0])]})});var subQ4=sQuery(id+"F23.wireOp",EDGE,"E34");Q23=makeQuery(id+"FQKKJbCCAw18BRu_1.9.F26.boolean.opBoolean","INTERSECT",EDGE,{"disambiguationData":[OD(1.0)],"derivedFrom":[makeQuery(id+"FQKKJbCCAw18BRu_1.8.F26.boolean.opBoolean","SPLIT",FACE,{"disambiguationData":[TD([subQ3])],"derivedFrom":makeQuery(id+"FQKKJbCCAw18BRu_1.7.F26.boolean.opBoolean","SPLIT",FACE,{"disambiguationData":[TD([subQ3])],"derivedFrom":makeQuery(id+"FQKKJbCCAw18BRu_1.6.F26.boolean.opBoolean","SPLIT",FACE,{"disambiguationData":[TD([subQ3])],"derivedFrom":makeQuery(id+"FQKKJbCCAw18BRu_1.5.F26.boolean.opBoolean","SPLIT",FACE,{"disambiguationData":[TD([subQ3])],"derivedFrom":makeQuery(id+"FQKKJbCCAw18BRu_1.4.F26.boolean.opBoolean","SPLIT",FACE,{"disambiguationData":[TD([subQ3])],"derivedFrom":makeQuery(id+"FQKKJbCCAw18BRu_1.3.F26.boolean.opBoolean","SPLIT",FACE,{"disambiguationData":[TD([subQ3])],"derivedFrom":makeQuery(id+"FQKKJbCCAw18BRu_1.2.F26.boolean.opBoolean","SPLIT",FACE,{"disambiguationData":[TD([subQ3])],"derivedFrom":makeQuery(id+"FQKKJbCCAw18BRu_1.1.F26.boolean.opBoolean","SPLIT",FACE,{"disambiguationData":[OD(0.0)],"derivedFrom":makeQuery(id+"F24.opExtrude","CAP_FACE",FACE,{"disambiguationData":[OSD([subQ1,subQ4])],"isStart":false})})})})})})})})}),makeQuery(id+"FQKKJbCCAw18BRu_1.9.F26.opExtrude","SWEPT_FACE",FACE,{"disambiguationData":[OSD([subQ0])]})]});}
            fillet(context, id + "F29", {"entities" : qUnion([Q0, Q1, Q2, Q3, Q4, Q5, Q6, Q7, Q8, Q9, Q10, Q11, Q12, Q13, Q14, Q15, Q16, Q17, Q18, Q19, Q20, Q21, Q22, Q23]), "radius" : 1 * mm, "tangentPropagation" : true, "allowEdgeOverflow" : false});
        }
        {
            var Q0;
            Q0=qCreatedBy(makeId("Top.planeOp"),FACE);
            var sketch = newSketch(context, id + "F30", { "sketchPlane" : qUnion([Q0])});
            skCircle(sketch, "E38", {"center": v(-55.86, 32.25) * mm, "radius": 4.75 * mm});
            skCircle(sketch, "E39", {"center": v(-55.86, 32.25) * mm, "radius": 8 * mm});
            skLineSegment(sketch, "E40", {"start": v(0, 0) * mm, "end": v(-55.86, 32.25) * mm, "construction": true});
            skSolve(sketch);
        }
        {
            var Q0;
            Q0=makeQuery(id+"F30.imprint","IMPRINT",FACE,{"disambiguationData":[TD([[makeQuery(id+"F30.imprint","IMPRINT",EDGE,{"derivedFrom":sQuery(id+"F30.wireOp",EDGE,"E38")}),-1.0]])]});
            extrude(context, id + "F31", {"entities" : qUnion([Q0]), "operationType" : NewBodyOperationType.ADD, "depth" : 20 * mm, "offsetDistance" : 25 * mm, "hasSecondDirection" : true, "secondDirectionOppositeDirection" : false, "secondDirectionDepth" : 5 * mm});
        }
        {
            var Q0;
            {var subQ3=sQuery(id+"F6.wireOp",EDGE,"E12");var subQ8=sQuery(id+"F0.wireOp",EDGE,"E4");var subQ10=makeQuery(id+"F7.opExtrude","SWEPT_FACE",FACE,{"disambiguationData":[OSD([subQ3])]});var subQ11=sQuery(id+"F0.wireOp",EDGE,"E3");var subQ12=sQuery(id+"F0.wireOp",EDGE,"E1");var subQ13=makeQuery(id+"F1.opExtrude","CAP_FACE",FACE,{"disambiguationData":[OSD([subQ12,subQ11,subQ8])],"isStart":false});Q0=makeQuery(id+"F24.boolean.opBoolean","SPLIT",FACE,{"disambiguationData":[TD([makeQuery(id+"F1.opExtrude","SWEPT_FACE",FACE,{"disambiguationData":[OSD([subQ11])]})])],"derivedFrom":makeQuery(id+"FA8SAaLpnDRHzi7_1.2.F7.boolean.opBoolean","MERGE",FACE,{"derivedFrom":[makeQuery(id+"FA8SAaLpnDRHzi7_1.1.F7.boolean.opBoolean","MERGE",FACE,{"derivedFrom":[makeQuery(id+"F7.boolean.opBoolean","MERGE",FACE,{"derivedFrom":[subQ13,subQ10]}),makeQuery(id+"FA8SAaLpnDRHzi7_1.1.F7.opExtrude","SWEPT_FACE",FACE,{"disambiguationData":[OSD([subQ3])]})]}),makeQuery(id+"FA8SAaLpnDRHzi7_1.2.F7.opExtrude","SWEPT_FACE",FACE,{"disambiguationData":[OSD([subQ3])]})]})});}
            var sketch = newSketch(context, id + "F32", { "sketchPlane" : qUnion([Q0])});
            skCircle(sketch, "E41", {"center": v(0, 64.5) * mm, "radius": 4.75 * mm});
            skCircle(sketch, "E42", {"center": v(0, 64.5) * mm, "radius": 8 * mm});
            skLineSegment(sketch, "E43", {"start": v(0, 64.5) * mm, "end": v(0, 0) * mm, "construction": true});
            skSolve(sketch);
        }
        {
            var Q0;
            Q0 = qSketchRegion(id + "F32", true);
            extrude(context, id + "F33", {"entities" : qUnion([Q0]), "operationType" : NewBodyOperationType.ADD, "depth" : 6 * mm, "offsetDistance" : 25 * mm});
        }
        {
            var Q0;
            Q0=makeQuery(id+"F31.opExtrude","CAP_EDGE",EDGE,{"disambiguationData":[OSD([sQuery(id+"F30.wireOp",EDGE,"E38")])],"isStart":false});
            var Q1;
            Q1=makeQuery(id+"F33.opExtrude","CAP_EDGE",EDGE,{"disambiguationData":[OSD([sQuery(id+"F32.wireOp",EDGE,"E41")])],"isStart":false});
            fillet(context, id + "F34", {"entities" : qUnion([Q0, Q1]), "radius" : 2 * mm, "tangentPropagation" : true, "allowEdgeOverflow" : false});
        }
        {
            var Q0;
            {var subQ3=sQuery(id+"F6.wireOp",EDGE,"E12");var subQ8=sQuery(id+"F0.wireOp",EDGE,"E4");var subQ10=makeQuery(id+"F7.opExtrude","SWEPT_FACE",FACE,{"disambiguationData":[OSD([subQ3])]});var subQ11=sQuery(id+"F0.wireOp",EDGE,"E3");var subQ12=sQuery(id+"F0.wireOp",EDGE,"E1");var subQ13=makeQuery(id+"F1.opExtrude","CAP_FACE",FACE,{"disambiguationData":[OSD([subQ12,subQ11,subQ8])],"isStart":false});Q0=makeQuery(id+"F31.boolean.opBoolean","INTERSECT",EDGE,{"derivedFrom":[makeQuery(id+"F24.boolean.opBoolean","SPLIT",FACE,{"disambiguationData":[TD([makeQuery(id+"F1.opExtrude","SWEPT_FACE",FACE,{"disambiguationData":[OSD([subQ11])]})])],"derivedFrom":makeQuery(id+"FA8SAaLpnDRHzi7_1.2.F7.boolean.opBoolean","MERGE",FACE,{"derivedFrom":[makeQuery(id+"FA8SAaLpnDRHzi7_1.1.F7.boolean.opBoolean","MERGE",FACE,{"derivedFrom":[makeQuery(id+"F7.boolean.opBoolean","MERGE",FACE,{"derivedFrom":[subQ13,subQ10]}),makeQuery(id+"FA8SAaLpnDRHzi7_1.1.F7.opExtrude","SWEPT_FACE",FACE,{"disambiguationData":[OSD([subQ3])]})]}),makeQuery(id+"FA8SAaLpnDRHzi7_1.2.F7.opExtrude","SWEPT_FACE",FACE,{"disambiguationData":[OSD([subQ3])]})]})}),makeQuery(id+"F31.opExtrude","SWEPT_FACE",FACE,{"disambiguationData":[OSD([sQuery(id+"F30.wireOp",EDGE,"E39")])]})]});}
            fillet(context, id + "F35", {"entities" : qUnion([Q0]), "radius" : 2 * mm, "tangentPropagation" : true, "allowEdgeOverflow" : false});
        }
    });
